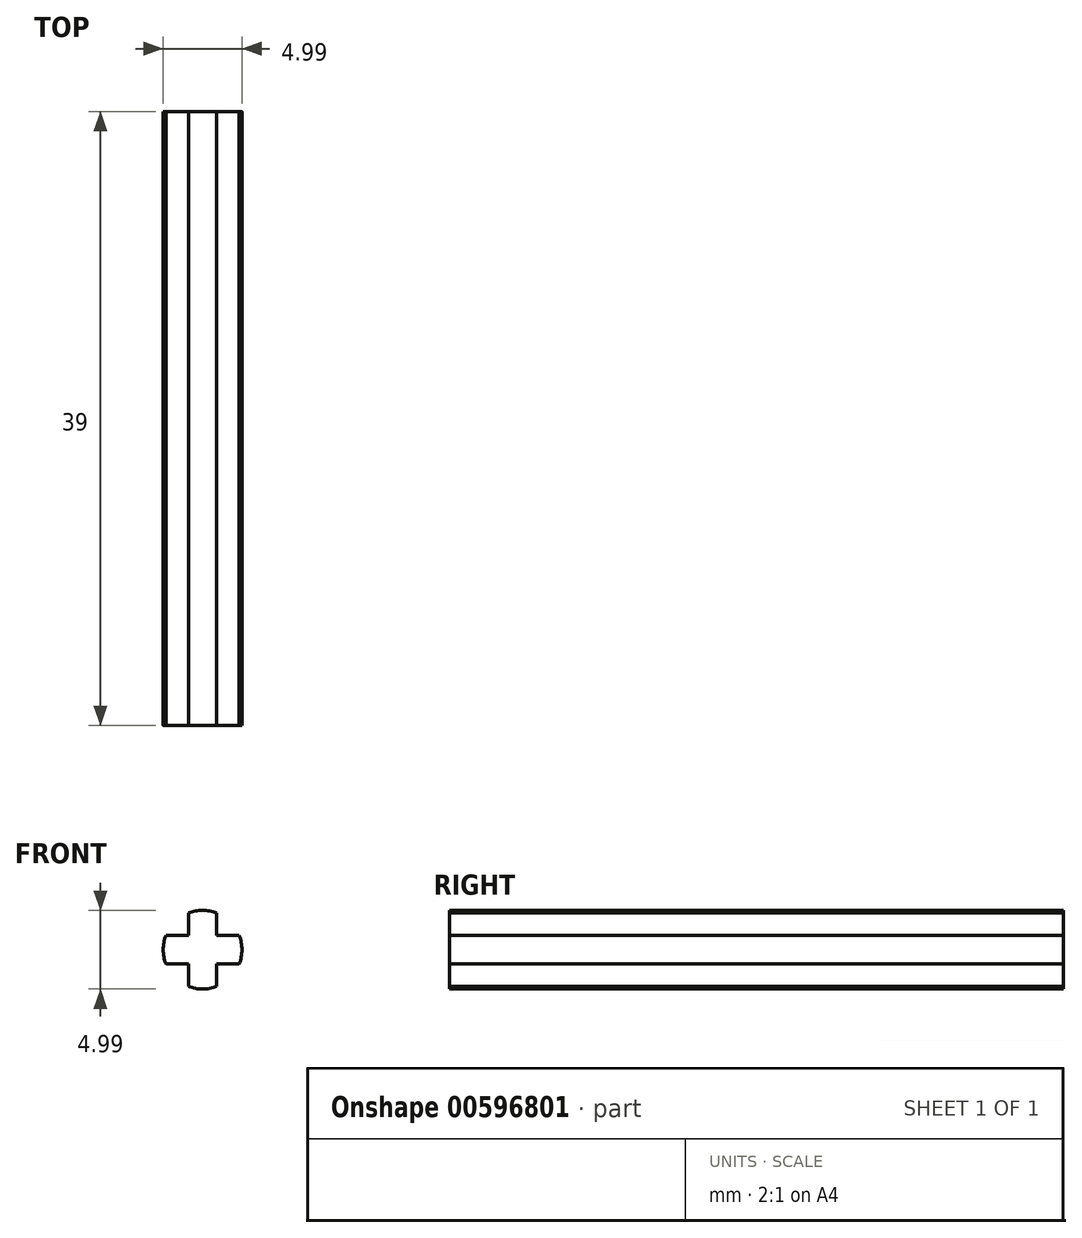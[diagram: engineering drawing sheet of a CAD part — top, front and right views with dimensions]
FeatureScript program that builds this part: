
annotation { "Feature Type Name" : "Feature", "Feature Type Description" : "" }
export const myFeature = defineFeature(function(context is Context, id is Id, definition is map)
    precondition{}
    {
        {
            var Q0;
            Q0=qCreatedBy(makeId("Front.planeOp"),FACE);
            var sketch = newSketch(context, id + "F0", { "sketchPlane" : qUnion([Q0])});
            skArc(sketch, "E0", {"start": v(2.12, -0.83) * mm, "mid": v(2.28, 0.07) * mm, "end": v(2.12, 0.97) * mm});
            skLineSegment(sketch, "E1.left", {"start": v(-1.12, 2.4) * mm, "end": v(-1.12, 0.97) * mm});
            skLineSegment(sketch, "E1.right", {"start": v(0.68, 2.4) * mm, "end": v(0.68, 0.97) * mm});
            skLineSegment(sketch, "E2.bottom", {"start": v(2.12, 0.97) * mm, "end": v(0.68, 0.97) * mm});
            skLineSegment(sketch, "E2.top", {"start": v(2.12, -0.83) * mm, "end": v(0.68, -0.83) * mm});
            skArc(sketch, "E3.trimOffspring", {"start": v(0.68, 2.4) * mm, "mid": v(-0.22, 2.57) * mm, "end": v(-1.12, 2.4) * mm});
            skArc(sketch, "E4.trimOffspring", {"start": v(-2.55, 0.97) * mm, "mid": v(-2.71, 0.07) * mm, "end": v(-2.55, -0.83) * mm});
            skArc(sketch, "E5.trimOffspring", {"start": v(-1.12, -2.26) * mm, "mid": v(-0.22, -2.42) * mm, "end": v(0.68, -2.26) * mm});
            skLineSegment(sketch, "E6.trimOffspring", {"start": v(-1.12, -0.83) * mm, "end": v(-1.12, -2.26) * mm});
            skLineSegment(sketch, "E7.trimOffspring", {"start": v(-1.12, 0.97) * mm, "end": v(-2.55, 0.97) * mm});
            skLineSegment(sketch, "E8.trimOffspring", {"start": v(0.68, -0.83) * mm, "end": v(0.68, -2.26) * mm});
            skLineSegment(sketch, "E9.trimOffspring", {"start": v(-1.12, -0.83) * mm, "end": v(-2.55, -0.83) * mm});
            skSolve(sketch);
        }
        {
            var Q0;
            Q0=qSketchRegion(id+"F0",true);
            extrude(context, id + "F1", {"entities" : qUnion([Q0]), "endBound" : BoundingType.SYMMETRIC, "depth" : 39 * mm, "offsetDistance" : 25 * mm});
        }
    });
